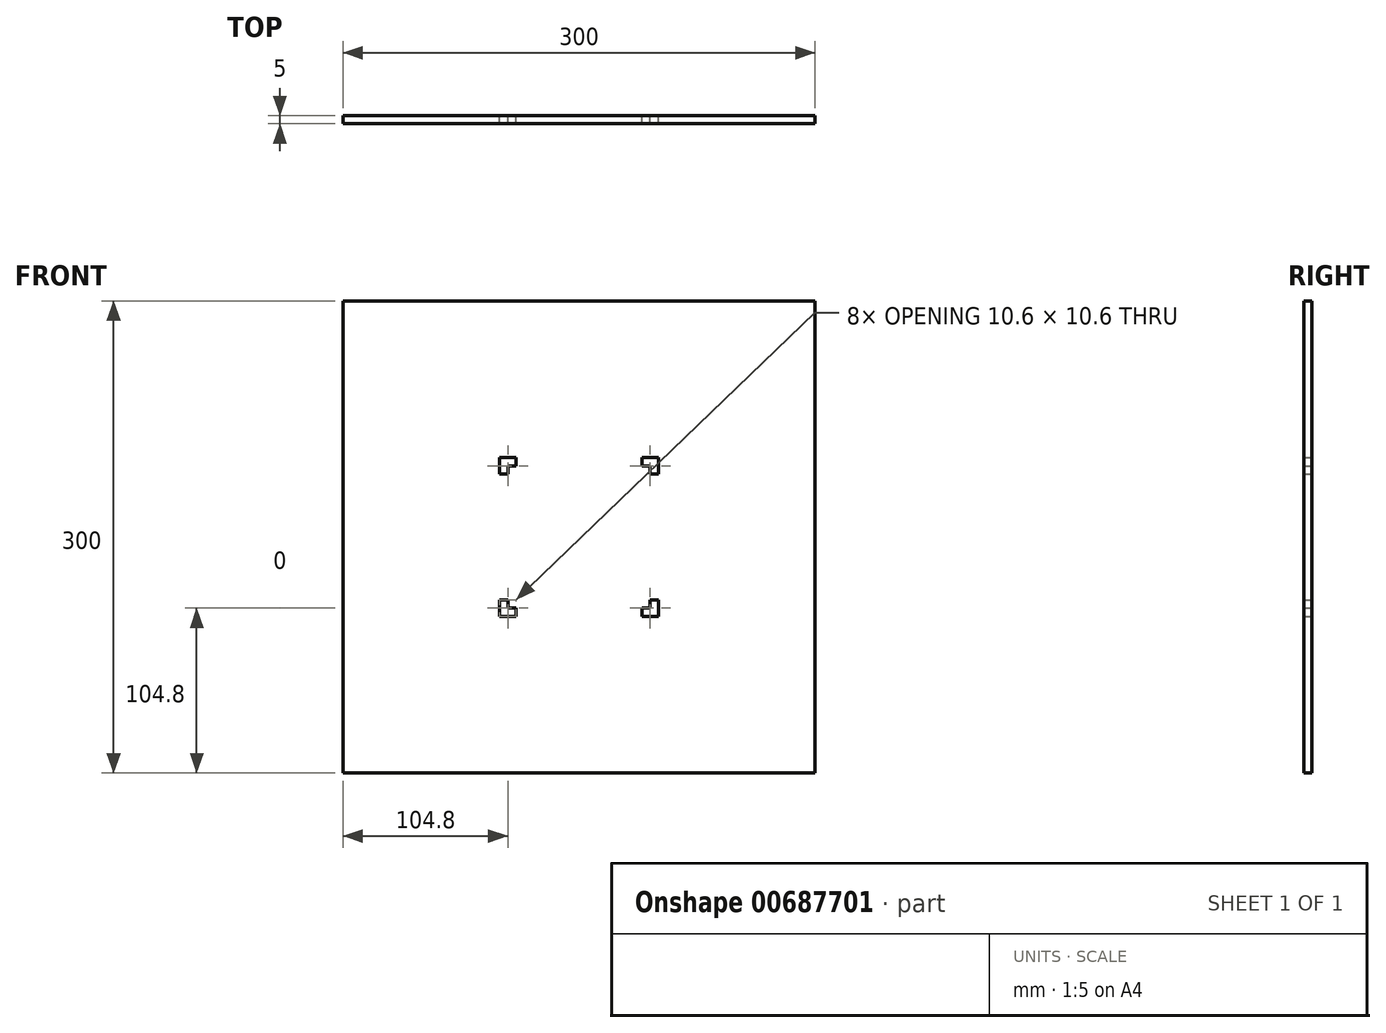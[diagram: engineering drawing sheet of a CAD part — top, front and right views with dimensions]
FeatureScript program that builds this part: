
annotation { "Feature Type Name" : "Feature", "Feature Type Description" : "" }
export const myFeature = defineFeature(function(context is Context, id is Id, definition is map)
    precondition{}
    {
        {
            var Q0;
            Q0=qCreatedBy(makeId("Front.planeOp"),FACE);
            var sketch = newSketch(context, id + "F0", { "sketchPlane" : qUnion([Q0])});
            skLineSegment(sketch, "E0.bottom", {"start": v(-150, 150) * mm, "end": v(150, 150) * mm});
            skLineSegment(sketch, "E0.top", {"start": v(-150, -150) * mm, "end": v(150, -150) * mm});
            skLineSegment(sketch, "E0.left", {"start": v(-150, 150) * mm, "end": v(-150, -150) * mm});
            skLineSegment(sketch, "E0.right", {"start": v(150, 150) * mm, "end": v(150, -150) * mm});
            skPoint(sketch, "E0.middle", {"position": v(0, 0) * mm});
            skLineSegment(sketch, "E1.bottom", {"start": v(-50.5, 50.5) * mm, "end": v(-39.9, 50.5) * mm});
            skLineSegment(sketch, "E1.top", {"start": v(-50.5, -50.5) * mm, "end": v(-39.9, -50.5) * mm});
            skLineSegment(sketch, "E1.left", {"start": v(-50.5, 50.5) * mm, "end": v(-50.5, 39.9) * mm});
            skLineSegment(sketch, "E1.right", {"start": v(50.5, 50.5) * mm, "end": v(50.5, 39.9) * mm});
            skLineSegment(sketch, "E2.bottom", {"start": v(-50.5, 50.5) * mm, "end": v(-45.2, 50.5) * mm});
            skLineSegment(sketch, "E2.top", {"start": v(-50.5, 39.9) * mm, "end": v(-45.2, 39.9) * mm});
            skLineSegment(sketch, "E2.right", {"start": v(-45.2, 45.2) * mm, "end": v(-45.2, 39.9) * mm});
            skPoint(sketch, "E3.oppositeSnap0", {"position": v(-45.2, 45.2) * mm});
            skLineSegment(sketch, "E3.top", {"start": v(-45.2, 45.2) * mm, "end": v(-39.9, 45.2) * mm});
            skLineSegment(sketch, "E3.left", {"start": v(-50.5, 50.5) * mm, "end": v(-50.5, 45.2) * mm});
            skLineSegment(sketch, "E3.right", {"start": v(-39.9, 50.5) * mm, "end": v(-39.9, 45.2) * mm});
            skLineSegment(sketch, "E4.bottom", {"start": v(50.5, 50.5) * mm, "end": v(45.2, 50.5) * mm});
            skLineSegment(sketch, "E4.top", {"start": v(50.5, 39.9) * mm, "end": v(45.2, 39.9) * mm});
            skLineSegment(sketch, "E4.right", {"start": v(45.2, 45.2) * mm, "end": v(45.2, 39.9) * mm});
            skLineSegment(sketch, "E5.bottom", {"start": v(39.9, 50.5) * mm, "end": v(50.5, 50.5) * mm});
            skLineSegment(sketch, "E5.top", {"start": v(39.9, 45.2) * mm, "end": v(45.2, 45.2) * mm});
            skLineSegment(sketch, "E5.left", {"start": v(39.9, 50.5) * mm, "end": v(39.9, 45.2) * mm});
            skLineSegment(sketch, "E5.right", {"start": v(50.5, 50.5) * mm, "end": v(50.5, 45.2) * mm});
            skLineSegment(sketch, "E6.bottom", {"start": v(-50.5, -50.5) * mm, "end": v(-45.2, -50.5) * mm});
            skLineSegment(sketch, "E6.top", {"start": v(-50.5, -39.9) * mm, "end": v(-45.2, -39.9) * mm});
            skLineSegment(sketch, "E6.left", {"start": v(-50.5, -50.5) * mm, "end": v(-50.5, -39.9) * mm});
            skLineSegment(sketch, "E6.right", {"start": v(-45.2, -45.2) * mm, "end": v(-45.2, -39.9) * mm});
            skLineSegment(sketch, "E7.bottom", {"start": v(-45.2, -45.2) * mm, "end": v(-39.9, -45.2) * mm});
            skLineSegment(sketch, "E7.left", {"start": v(-50.5, -45.2) * mm, "end": v(-50.5, -50.5) * mm});
            skLineSegment(sketch, "E7.right", {"start": v(-39.9, -45.2) * mm, "end": v(-39.9, -50.5) * mm});
            skLineSegment(sketch, "E8.bottom", {"start": v(39.9, -50.5) * mm, "end": v(50.5, -50.5) * mm});
            skLineSegment(sketch, "E8.top", {"start": v(39.9, -45.2) * mm, "end": v(45.2, -45.2) * mm});
            skLineSegment(sketch, "E8.left", {"start": v(39.9, -50.5) * mm, "end": v(39.9, -45.2) * mm});
            skLineSegment(sketch, "E8.right", {"start": v(50.5, -50.5) * mm, "end": v(50.5, -45.2) * mm});
            skLineSegment(sketch, "E9.bottom", {"start": v(50.5, -39.9) * mm, "end": v(45.2, -39.9) * mm});
            skLineSegment(sketch, "E9.top", {"start": v(50.5, -50.5) * mm, "end": v(45.2, -50.5) * mm});
            skLineSegment(sketch, "E9.left", {"start": v(50.5, -39.9) * mm, "end": v(50.5, -50.5) * mm});
            skLineSegment(sketch, "E9.right", {"start": v(45.2, -39.9) * mm, "end": v(45.2, -45.2) * mm});
            skLineSegment(sketch, "E10.trimOffspring", {"start": v(-50.5, -39.9) * mm, "end": v(-50.5, -50.5) * mm});
            skSolve(sketch);
        }
        {
            var Q0;
            Q0 = qSketchRegion(id + "F0", true);
            extrude(context, id + "F1", {"entities" : qUnion([Q0]), "depth" : 5 * mm, "offsetDistance" : 25 * mm});
        }
    });
